# Revit family: Ext-N-MDMF-36 x 84
name_source: partatom
category: Doors
revit_build: Autodesk Revit MEP 2014 (Build: 20130308_1515(x64)
units: mm (PartAtom-declared; Revit-internal decimal feet)

## types (1)
- Ext-N-MDMF-36" x 84"
    ADA Clearance Lines = No
    Analytic Construction = <None>
    Assembly Code = B2030120
    Cost = 0 $
    Description = Hollow Metal Door with Hollow Metal Frame
    Door Panel Height = 7' - 0"
    Door Panel Width = 3' - 0"
    Frame Height = 7' - 2"
    Frame Width = 3' - 4"
    Function = Exterior
    Height = 7' - 0"
    Leaf Width = 2' - 11 13/16"
    Model = Ext-N-MDMF-36" x 84"
    P1 Width = 3' - 2"
    R1 Height = 7' - 0"
    Rough Height = 7' - 2"
    Rough Width = 3' - 4"
    SDI Door Bottom Rail Width = 5' - 0"
    SDI Door Configuration = SG
    SDI Door Finish Color = Prime
    SDI Door Finish Type = Painted
    SDI Door Glass Type = 1/4" Tempered
    SDI Door Material = Paint - Generic - Prime
    SDI Door Material Type = Hollow Metal
    SDI Door Panel Type = N
    SDI Door Stile Width = 0' - 6"
    SDI Door Top Rail Width = 0' - 7 3/4"
    SDI Family Version = 1.0
    SDI Frame Finish Color = Prime
    SDI Frame Finish Type = Painted
    SDI Frame Head Width = 0' - 2"
    SDI Frame Jamb Width = 0' - 2"
    SDI Frame Material = Paint - Generic - Prime
    SDI Frame Material Type = Hollow Metal
    SDI Frame Type = 3 Piece
    SDI Glass Material = Glass
    SDI Panel 1 Width = 3' - 0"
    SDI RO Spacing = 0' - 0"
    Thickness = 0' - 1 3/4"
    Type Comments = EXT,
    Width = 3' - 0"

## geometry (parser evidence)
native form markers: Sweep x1
no freeform markers — native parametric forms only
